# Revit family: Trap-BottleTrap-ForBasins-Symmetric-WithRosette-Vitra-Other-A45159
name_source: partatom
category: Plumbing Fixtures
revit_build: Autodesk Revit 2017 (Build: 20160225_1515(x64)
units: mm (PartAtom-declared; Revit-internal decimal feet)

## family parameters
Cut with Voids When Loaded = No
Host = Face
OmniClass Number = 23.45.55.17
OmniClass Title = Mixing Faucets
Part Type = Normal
Room Calculation Point = No
Round Connector Dimension = Use Diameter
Shared = Yes

## types (9) — shared parameters
BIMobject category = Sanitary - Taps & Mixers
CW Connection = Yes
Default Elevation = 600 mm
Depth(mm) = 455 mm
Description = Washbasin Siphon Set - Symmetrical - Rosette
Design country = Turkey
HW Connection = Yes
Height(mm) = 144 mm  [stored 0.472441 ft]
IFC Classification = Sanitary Terminal
Manufacturer = Vitra
Manufacturer name = Vitra
Masterformat 2014 Code = 22 13 16
Masterformat 2014 Description = Sanitary Waste and Vent Piping
MountingType = Wall Mounted
NBS Referans Code = 31-76
NBS Referans Description = Sanitary Dispensing And Disposal Units
Nominal height = 0.000
Nominal width = 0.000
Number Of Connections = 3 mm  [stored 0.00984252 ft]
OmniClass Code = 23-21 23 27
OmniClass Description = Residential Waste Disposal Units
Product Type = Washbasin Siphon Set
Product certification = https://vitraglobal.com
Product data url = https://www.vitra.com.tr
Product family = Other
Product group = Other Trap
Technical description = https://www.vitra.com.tr
UNSPSC Code = 301815
UNSPSC Description = Sanitary ware
URL = https://vitraglobal.com
Uniclass 1.4 Code = L7218
Uniclass 1.4 Description = Sanitary disposal units
Uniclass 2.0 Code = PR-31-76
Uniclass 2.0 Description = Sanitary Dispensing And Disposal Units
Uniclass 2015 Code = Pr_60_45_90
Uniclass 2015 Name = Wastewater and water mixer products
Uniformat II Code = D2010
Uniformat II Description = Plumbing Fixtures
Waste Connection = Yes
Weight Net (kg) = 1,775
Width(mm) = 170 mm  [stored 0.557743 ft]
Youtube = https://www.youtube.com
zero-valued in all types: Cost

## per-type parameters (varying)
| type | Article No. (default) | Coating Material | Color | Connection Diameter (mm) | Model | Product SKU | Warranty Period (Year) |
| Trap-BottleTrap-ForBasins-Symmetric-WithRosette-Vitra-Other-A45159 | A45159 | Chrome | Chrome | 10 mm  [stored 0.0328084 ft] | A45159 | A45159 | 10 Years |
| Trap-BottleTrap-ForBasins-Symmetric-WithRosette-Vitra-Other-A4515926 | A4515926 | BrightCopper | Copper | 10 mm  [stored 0.0328084 ft] | A4515926 | A4515926 | 10 Years |
| Trap-BottleTrap-ForBasins-Symmetric-WithRosette-Vitra-Other-A4515926IND | A4515926IND | BrightCopper | Copper | 15 mm  [stored 0.0492126 ft] | A4515926IND | A4515926IND | 5 Years |
| Trap-BottleTrap-ForBasins-Symmetric-WithRosette-Vitra-Other-A4515934 | A4515934 | BrushedNickel | Chrome | 10 mm  [stored 0.0328084 ft] | A4515934 | A4515934 | 10 Years |
| Trap-BottleTrap-ForBasins-Symmetric-WithRosette-Vitra-Other-A4515934IND | A4515934IND | BrushedNickel | Brushed Copper | 15 mm  [stored 0.0492126 ft] | A4515934IND | A4515934IND | 5 Years |
| Trap-BottleTrap-ForBasins-Symmetric-WithRosette-Vitra-Other-A4515936 | A4515936 | MatteBlack | Black | 10 mm  [stored 0.0328084 ft] | A4515936 | A4515936 | 10 Years |
| Trap-BottleTrap-ForBasins-Symmetric-WithRosette-Vitra-Other-A4515936IND | A4515936IND | MatteBlack | Black | 15 mm  [stored 0.0492126 ft] | A4515936IND | A4515936IND | 5 Years |
| Trap-BottleTrap-ForBasins-Symmetric-WithRosette-Vitra-Other-A45159EXP | A45159EXP | Chrome | Chrome | 10 mm  [stored 0.0328084 ft] | A45159EXP | A45159EXP | 5 Years |
| Trap-BottleTrap-ForBasins-Symmetric-WithRosette-Vitra-Other-A45159IND | A45159IND | Chrome | Chrome | 15 mm  [stored 0.0492126 ft] | A45159IND | A45159IND | 5 Years |

note: [stored X ft] marks values corroborated as IEEE doubles in the binary element streams (Revit-internal decimal feet)

## geometry (parser evidence)
native form markers: Sweep x3
no freeform markers — native parametric forms only
